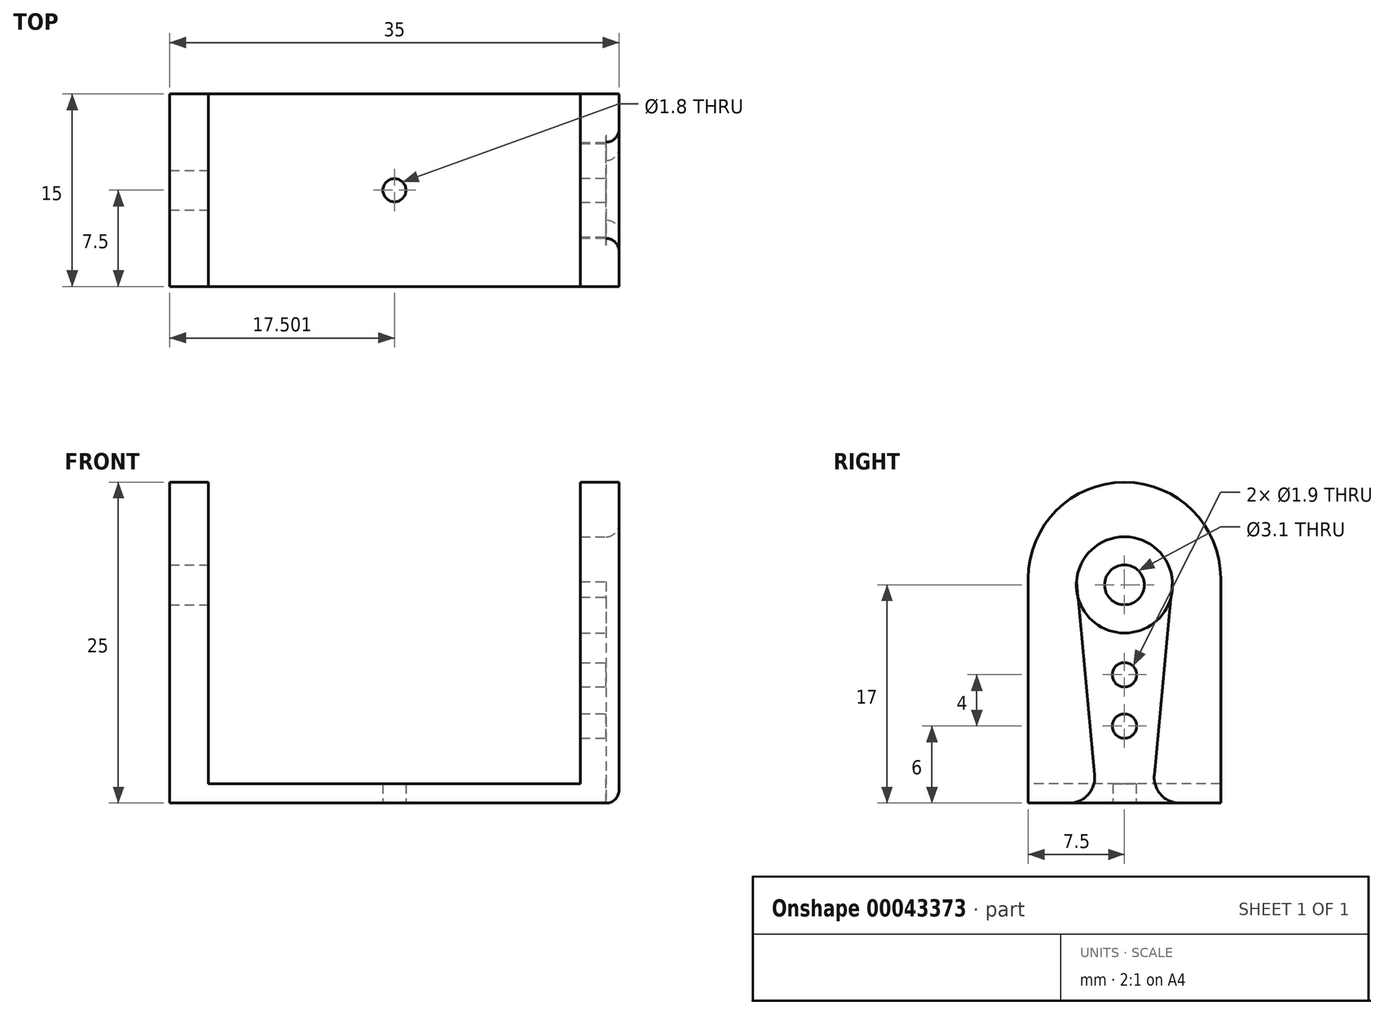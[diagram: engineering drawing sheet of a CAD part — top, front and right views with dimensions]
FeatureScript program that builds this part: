
annotation { "Feature Type Name" : "Feature", "Feature Type Description" : "" }
export const myFeature = defineFeature(function(context is Context, id is Id, definition is map)
    precondition{}
    {
        {
            var Q0;
            Q0=qCreatedBy(makeId("Top.planeOp"),FACE);
            var sketch = newSketch(context, id + "F0", { "sketchPlane" : qUnion([Q0])});
            skLineSegment(sketch, "E0.bottom", {"start": v(-4.1, 6.75) * mm, "end": v(26.9, 6.75) * mm});
            skLineSegment(sketch, "E0.top", {"start": v(-4.1, -8.25) * mm, "end": v(26.9, -8.25) * mm});
            skLineSegment(sketch, "E0.left", {"start": v(-4.1, 6.75) * mm, "end": v(-4.1, -8.25) * mm});
            skLineSegment(sketch, "E0.right", {"start": v(26.9, 6.75) * mm, "end": v(26.9, -8.25) * mm});
            skLineSegment(sketch, "E1", {"start": v(24.9, 6.75) * mm, "end": v(24.9, -8.25) * mm});
            skLineSegment(sketch, "E2.trimOffspring", {"start": v(24.9, -0.75) * mm, "end": v(26.9, -0.75) * mm, "construction": true});
            skPoint(sketch, "E3.orphan", {"position": v(-4.1, -0.75) * mm});
            skLineSegment(sketch, "E4", {"start": v(-4.1, -0.75) * mm, "end": v(24.9, -0.75) * mm, "construction": true});
            skLineSegment(sketch, "E5", {"start": v(-4.1, 6.75) * mm, "end": v(24.9, -8.25) * mm, "construction": true});
            skPoint(sketch, "E6", {"position": v(10.4, -0.75) * mm});
            skLineSegment(sketch, "E7.bottom", {"start": v(-4.1, 6.75) * mm, "end": v(-7.1, 6.75) * mm});
            skLineSegment(sketch, "E7.top", {"start": v(-4.1, -8.25) * mm, "end": v(-7.1, -8.25) * mm});
            skLineSegment(sketch, "E7.right", {"start": v(-7.1, 6.75) * mm, "end": v(-7.1, -8.25) * mm});
            skCircle(sketch, "E8", {"center": v(10.4, -0.75) * mm, "radius": 0.9 * mm});
            skSolve(sketch);
        }
        {
            var Q0;
            {var subQ1=sQuery(id+"F0.wireOp",EDGE,"E1");Q0=makeQuery(id+"F0.imprint","IMPRINT",FACE,{"disambiguationData":[TD([[makeQuery(id+"F0.imprint","IMPRINT",EDGE,{"derivedFrom":subQ1}),-1.0]])]});}
            extrude(context, id + "F1", {"entities" : qUnion([Q0]), "depth" : 1.5 * mm});
        }
        {
            var Q0;
            {var subQ1=sQuery(id+"F0.wireOp",EDGE,"E0.right");Q0=makeQuery(id+"F0.imprint","IMPRINT",FACE,{"disambiguationData":[TD([[makeQuery(id+"F0.imprint","IMPRINT",EDGE,{"derivedFrom":subQ1}),-1.0]])]});}
            var Q1;
            Q1=makeQuery(id+"F0.imprint","IMPRINT",FACE,{"disambiguationData":[TD([[makeQuery(id+"F0.imprint","IMPRINT",EDGE,{"derivedFrom":sQuery(id+"F0.wireOp",EDGE,"E7.bottom")}),1.0]])]});
            extrude(context, id + "F2", {"entities" : qUnion([Q0, Q1]), "operationType" : NewBodyOperationType.ADD, "depth" : 25 * mm});
        }
        {
            var Q0;
            Q0=makeQuery(id+"F2.opExtrude","SWEPT_FACE",FACE,{"disambiguationData":[OSD([sQuery(id+"F0.wireOp",EDGE,"E0.right")])]});
            var sketch = newSketch(context, id + "F3", { "sketchPlane" : qUnion([Q0])});
            skLineSegment(sketch, "E9.bottom", {"start": v(-8.25, 25) * mm, "end": v(6.75, 25) * mm, "construction": true});
            skLineSegment(sketch, "E9.top", {"start": v(-8.25, 0) * mm, "end": v(6.75, 0) * mm, "construction": true});
            skLineSegment(sketch, "E9.left", {"start": v(-8.25, 25) * mm, "end": v(-8.25, 0) * mm, "construction": true});
            skLineSegment(sketch, "E9.right", {"start": v(6.75, 25) * mm, "end": v(6.75, 0) * mm, "construction": true});
            skLineSegment(sketch, "E10", {"start": v(-0.75, 25) * mm, "end": v(-0.75, 0) * mm, "construction": true});
            skCircle(sketch, "E11", {"center": v(-0.75, 17) * mm, "radius": 3.75 * mm});
            skCircle(sketch, "E12", {"center": v(-0.75, 10) * mm, "radius": 0.95 * mm});
            skCircle(sketch, "E13", {"center": v(-0.75, 17) * mm, "radius": 3 * mm, "construction": true});
            skPoint(sketch, "E14.center.orphan", {"position": v(-0.75, 6) * mm});
            skCircle(sketch, "E15", {"center": v(-0.75, 6) * mm, "radius": 0.95 * mm});
            skLineSegment(sketch, "E16.bottom", {"start": v(-8.25, 25) * mm, "end": v(6.75, 25) * mm});
            skLineSegment(sketch, "E16.top", {"start": v(-8.25, 0) * mm, "end": v(6.75, 0) * mm});
            skLineSegment(sketch, "E16.left", {"start": v(-8.25, 25) * mm, "end": v(-8.25, 0) * mm});
            skLineSegment(sketch, "E16.right", {"start": v(6.75, 25) * mm, "end": v(6.75, 0) * mm});
            skLineSegment(sketch, "E17", {"start": v(-2.75, -1.25) * mm, "end": v(1.25, -1.25) * mm});
            skPoint(sketch, "E18", {"position": v(-0.75, -1.25) * mm});
            skPoint(sketch, "E19.trimOffspring.end.orphan", {"position": v(3, 17) * mm});
            skLineSegment(sketch, "E20", {"start": v(-4.5, 17.25) * mm, "end": v(3, 17.25) * mm, "construction": true});
            skLineSegment(sketch, "E21", {"start": v(3, 17.25) * mm, "end": v(1.25, -1.25) * mm});
            skLineSegment(sketch, "E22", {"start": v(-4.5, 17.25) * mm, "end": v(-2.75, -1.25) * mm});
            skPoint(sketch, "E23", {"position": v(-0.75, 17.25) * mm});
            skCircle(sketch, "E24", {"center": v(-0.75, 17) * mm, "radius": 1.55 * mm});
            skSolve(sketch);
        }
        {
            var Q0;
            Q0=makeQuery(id+"F3.imprint","IMPRINT",FACE,{"disambiguationData":[TD([[makeQuery(id+"F3.imprint","IMPRINT",EDGE,{"derivedFrom":sQuery(id+"F3.wireOp",EDGE,"E15")}),1.0]])]});
            var Q1;
            Q1=makeQuery(id+"F3.imprint","IMPRINT",FACE,{"disambiguationData":[TD([[makeQuery(id+"F3.imprint","IMPRINT",EDGE,{"derivedFrom":sQuery(id+"F3.wireOp",EDGE,"E12")}),1.0]])]});
            var Q2;
            Q2=makeQuery(id+"F3.imprint","IMPRINT",FACE,{"disambiguationData":[TD([[makeQuery(id+"F3.imprint","IMPRINT",EDGE,{"derivedFrom":sQuery(id+"F3.wireOp",EDGE,"E24")}),1.0]])]});
            var Q3;
            Q3=makeQuery(id+"F3.imprint","IMPRINT",FACE,{"disambiguationData":[TD([[makeQuery(id+"F3.imprint","IMPRINT",EDGE,{"derivedFrom":sQuery(id+"F3.wireOp",EDGE,"E24")}),-1.0]])]});
            extrude(context, id + "F4", {"entities" : qUnion([Q0, Q1, Q2, Q3]), "operationType" : NewBodyOperationType.REMOVE, "oppositeDirection" : true, "depth" : 3 * mm});
        }
        {
            var Q0;
            Q0=makeQuery(id+"F3.imprint","IMPRINT",FACE,{"disambiguationData":[TD([[makeQuery(id+"F3.imprint","IMPRINT",EDGE,{"derivedFrom":sQuery(id+"F3.wireOp",EDGE,"E24")}),1.0]])]});
            extrude(context, id + "F5", {"entities" : qUnion([Q0]), "operationType" : NewBodyOperationType.REMOVE, "oppositeDirection" : true, "depth" : 40 * mm});
        }
        {
            var Q0;
            Q0=makeQuery(id+"F3.imprint","IMPRINT",FACE,{"disambiguationData":[TD([[makeQuery(id+"F3.imprint","IMPRINT",EDGE,{"derivedFrom":sQuery(id+"F3.wireOp",EDGE,"E16.bottom")}),1.0]])]});
            extrude(context, id + "F6", {"entities" : qUnion([Q0]), "operationType" : NewBodyOperationType.ADD, "depth" : 1 * mm});
        }
        {
            var Q0;
            Q0=makeQuery(id+"F6.opExtrude","SWEPT_EDGE",EDGE,{"disambiguationData":[OSD([sQuery(id+"F3.wireOp",EDGE,"E17"),sQuery(id+"F3.wireOp",EDGE,"E22")])]});
            var Q1;
            Q1=makeQuery(id+"F6.opExtrude","SWEPT_EDGE",EDGE,{"disambiguationData":[OSD([sQuery(id+"F3.wireOp",EDGE,"E17"),sQuery(id+"F3.wireOp",EDGE,"E21")])]});
            fillet(context, id + "F7", {"entities" : qUnion([Q0, Q1]), "radius" : 2 * mm, "tangentPropagation" : true, "allowEdgeOverflow" : false});
        }
        {
            var Q0;
            Q0=makeQuery(id+"F2.opExtrude","CAP_EDGE",EDGE,{"disambiguationData":[OSD([sQuery(id+"F0.wireOp",EDGE,"E0.bottom")])],"isStart":false});
            var Q1;
            Q1=makeQuery(id+"F2.opExtrude","CAP_EDGE",EDGE,{"disambiguationData":[OSD([sQuery(id+"F0.wireOp",EDGE,"E0.top")])],"isStart":false});
            var Q2;
            Q2=makeQuery(id+"F2.opExtrude","CAP_EDGE",EDGE,{"disambiguationData":[OSD([sQuery(id+"F0.wireOp",EDGE,"E7.top")])],"isStart":false});
            var Q3;
            Q3=makeQuery(id+"F2.opExtrude","CAP_EDGE",EDGE,{"disambiguationData":[OSD([sQuery(id+"F0.wireOp",EDGE,"E7.bottom")])],"isStart":false});
            fillet(context, id + "F8", {"entities" : qUnion([Q0, Q1, Q2, Q3]), "radius" : 7.5 * mm, "tangentPropagation" : true, "allowEdgeOverflow" : false});
        }
        {
            var Q0;
            Q0=makeQuery(id+"F6.opExtrude","CAP_EDGE",EDGE,{"disambiguationData":[OSD([sQuery(id+"F3.wireOp",EDGE,"E22")])],"isStart":false});
            var Q1;
            {var subQ0=sQuery(id+"F3.wireOp",EDGE,"E17");var subQ1=sQuery(id+"F3.wireOp",EDGE,"E22");Q1=makeQuery(id+"F7.opFillet","BLEND_EDGE",EDGE,{"blendedFrom":[makeQuery(id+"F6.opExtrude","SWEPT_EDGE",EDGE,{"disambiguationData":[OSD([subQ0,subQ1])]}),makeQuery(id+"F6.opExtrude","CAP_FACE",FACE,{"disambiguationData":[OSD([sQuery(id+"F3.wireOp",EDGE,"E11"),sQuery(id+"F3.wireOp",EDGE,"E16.bottom"),sQuery(id+"F3.wireOp",EDGE,"E16.top"),sQuery(id+"F3.wireOp",EDGE,"E16.left"),sQuery(id+"F3.wireOp",EDGE,"E16.right"),subQ0,sQuery(id+"F3.wireOp",EDGE,"E21"),subQ1])],"isStart":false})],"blendedInto":[makeQuery(id+"F6.opExtrude","CAP_FACE",FACE,{"disambiguationData":[OSD([sQuery(id+"F3.wireOp",EDGE,"E11"),sQuery(id+"F3.wireOp",EDGE,"E16.bottom"),sQuery(id+"F3.wireOp",EDGE,"E16.top"),sQuery(id+"F3.wireOp",EDGE,"E16.left"),sQuery(id+"F3.wireOp",EDGE,"E16.right"),subQ0,sQuery(id+"F3.wireOp",EDGE,"E21"),subQ1])],"isStart":false})]});}
            var Q2;
            Q2=makeQuery(id+"F6.opExtrude","CAP_EDGE",EDGE,{"disambiguationData":[OSD([sQuery(id+"F3.wireOp",EDGE,"E17")])],"isStart":false});
            var Q3;
            {var subQ0=sQuery(id+"F3.wireOp",EDGE,"E17");var subQ1=sQuery(id+"F3.wireOp",EDGE,"E21");Q3=makeQuery(id+"F7.opFillet","BLEND_EDGE",EDGE,{"blendedFrom":[makeQuery(id+"F6.opExtrude","SWEPT_EDGE",EDGE,{"disambiguationData":[OSD([subQ0,subQ1])]}),makeQuery(id+"F6.opExtrude","CAP_FACE",FACE,{"disambiguationData":[OSD([sQuery(id+"F3.wireOp",EDGE,"E11"),sQuery(id+"F3.wireOp",EDGE,"E16.bottom"),sQuery(id+"F3.wireOp",EDGE,"E16.top"),sQuery(id+"F3.wireOp",EDGE,"E16.left"),sQuery(id+"F3.wireOp",EDGE,"E16.right"),subQ0,subQ1,sQuery(id+"F3.wireOp",EDGE,"E22")])],"isStart":false})],"blendedInto":[makeQuery(id+"F6.opExtrude","CAP_FACE",FACE,{"disambiguationData":[OSD([sQuery(id+"F3.wireOp",EDGE,"E11"),sQuery(id+"F3.wireOp",EDGE,"E16.bottom"),sQuery(id+"F3.wireOp",EDGE,"E16.top"),sQuery(id+"F3.wireOp",EDGE,"E16.left"),sQuery(id+"F3.wireOp",EDGE,"E16.right"),subQ0,subQ1,sQuery(id+"F3.wireOp",EDGE,"E22")])],"isStart":false})]});}
            var Q4;
            Q4=makeQuery(id+"F6.opExtrude","CAP_EDGE",EDGE,{"disambiguationData":[OSD([sQuery(id+"F3.wireOp",EDGE,"E21")])],"isStart":false});
            var Q5;
            Q5=makeQuery(id+"F6.opExtrude","CAP_EDGE",EDGE,{"disambiguationData":[OSD([sQuery(id+"F3.wireOp",EDGE,"E11")])],"isStart":false});
            fillet(context, id + "F9", {"entities" : qUnion([Q0, Q1, Q2, Q3, Q4, Q5]), "radius" : 1 * mm, "tangentPropagation" : true, "allowEdgeOverflow" : false});
        }
    });
